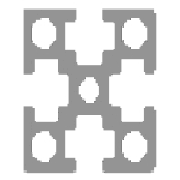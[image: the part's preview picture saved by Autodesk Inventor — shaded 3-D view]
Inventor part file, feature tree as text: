
AUTODESK INVENTOR PART (.ipt)
format: ipt  version: 2018.2 (Build 222227000, 227)  size: 264,704 bytes
history: native  units: mm
features: other x2, extrude x1
ambient origin geometry x8: Origin, YZ Plane, XZ Plane, XY Plane, X Axis, Y Axis, Z Axis, Center Point
bodies: Body1 (feature_tree)
feature tree (3):
  other  "開始平面"
  other  "終了平面"
  extrude  "ボディ"  Depth=4.0mm
